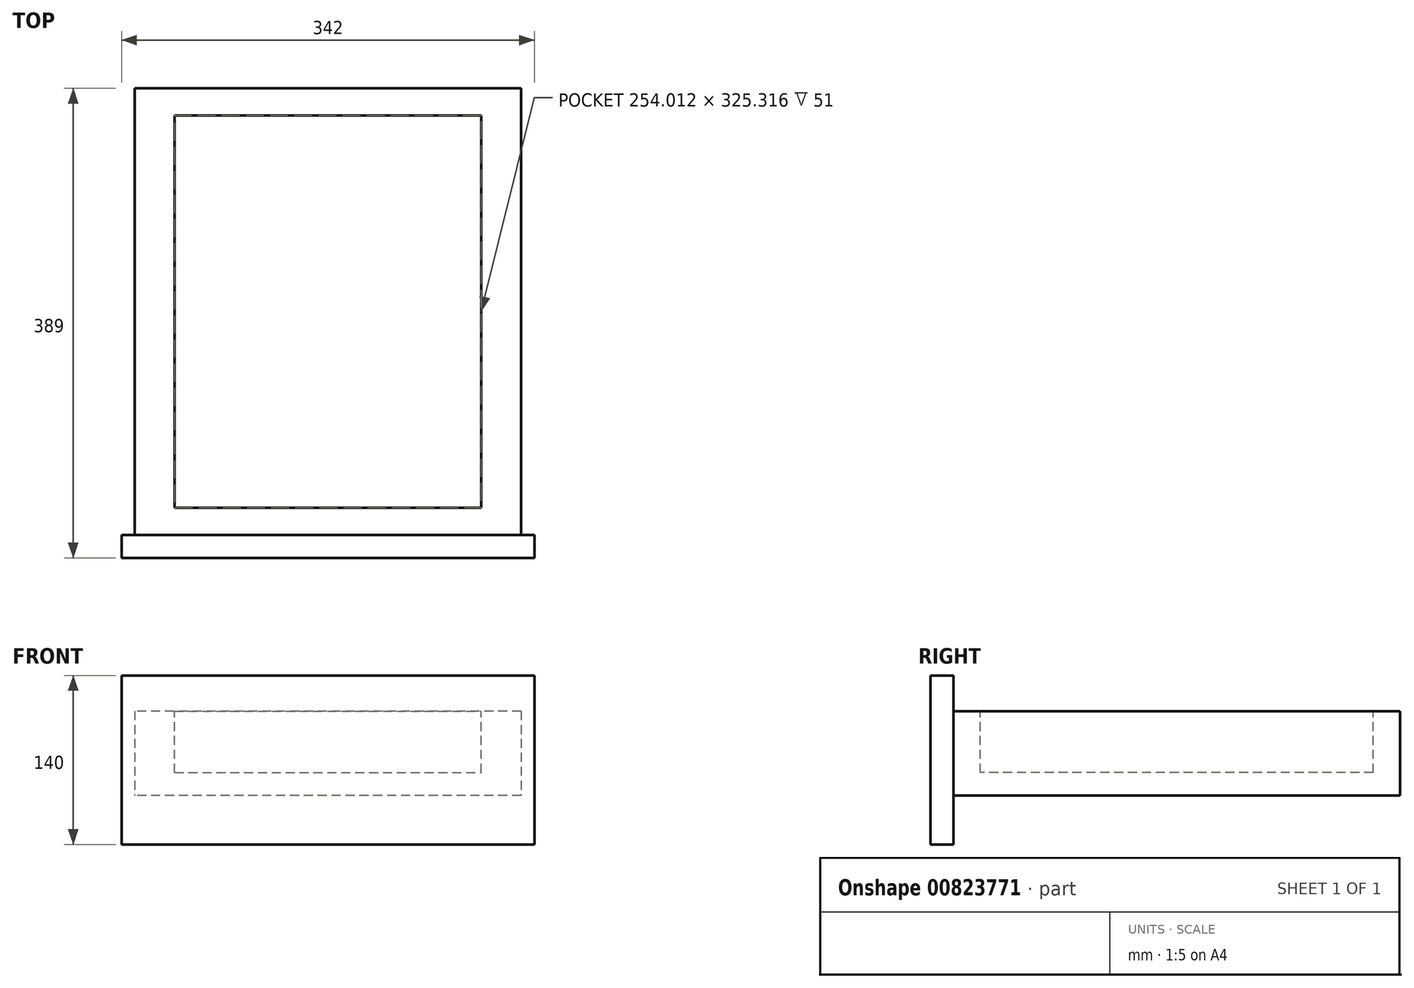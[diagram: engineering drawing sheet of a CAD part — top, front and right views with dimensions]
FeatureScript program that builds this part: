
annotation { "Feature Type Name" : "Feature", "Feature Type Description" : "" }
export const myFeature = defineFeature(function(context is Context, id is Id, definition is map)
    precondition{}
    {
        {
            var Q0;
            Q0=qCreatedBy(makeId("Top.planeOp"),FACE);
            var sketch = newSketch(context, id + "F0", { "sketchPlane" : qUnion([Q0])});
            skLineSegment(sketch, "E0.bottom", {"start": v(160, 185) * mm, "end": v(-160, 185) * mm});
            skLineSegment(sketch, "E0.top", {"start": v(160, -185) * mm, "end": v(-160, -185) * mm});
            skLineSegment(sketch, "E0.left", {"start": v(160, 185) * mm, "end": v(160, -185) * mm});
            skLineSegment(sketch, "E0.right", {"start": v(-160, 185) * mm, "end": v(-160, -185) * mm});
            skPoint(sketch, "E0.middle", {"position": v(0, 0) * mm});
            skSolve(sketch);
        }
        {
            var Q0;
            Q0=makeQuery(id+"F0.imprint","IMPRINT",FACE,{"disambiguationData":[TD([[makeQuery(id+"F0.imprint","IMPRINT",EDGE,{"derivedFrom":sQuery(id+"F0.wireOp",EDGE,"E0.bottom")}),1.0]])]});
            extrude(context, id + "F1", {"entities" : qUnion([Q0]), "depth" : 70 * mm, "offsetDistance" : 25 * mm});
        }
        {
            var Q0;
            Q0=makeQuery(id+"F1.opExtrude","CAP_FACE",FACE,{"disambiguationData":[OSD([sQuery(id+"F0.wireOp",EDGE,"E0.bottom"),sQuery(id+"F0.wireOp",EDGE,"E0.top"),sQuery(id+"F0.wireOp",EDGE,"E0.left"),sQuery(id+"F0.wireOp",EDGE,"E0.right")])],"isStart":false});
            var sketch = newSketch(context, id + "F2", { "sketchPlane" : qUnion([Q0])});
            skLineSegment(sketch, "E1.bottom", {"start": v(-127, 162.66) * mm, "end": v(127, 162.66) * mm});
            skLineSegment(sketch, "E1.top", {"start": v(-127, -162.66) * mm, "end": v(127, -162.66) * mm});
            skLineSegment(sketch, "E1.left", {"start": v(-127, 162.66) * mm, "end": v(-127, -162.66) * mm});
            skLineSegment(sketch, "E1.right", {"start": v(127, 162.66) * mm, "end": v(127, -162.66) * mm});
            skPoint(sketch, "E1.middle", {"position": v(0, 0) * mm});
            skSolve(sketch);
        }
        {
            var Q0;
            Q0=makeQuery(id+"F2.imprint","IMPRINT",FACE,{"disambiguationData":[TD([[makeQuery(id+"F2.imprint","IMPRINT",EDGE,{"derivedFrom":sQuery(id+"F2.wireOp",EDGE,"E1.bottom")}),-1.0]])]});
            extrude(context, id + "F3", {"entities" : qUnion([Q0]), "operationType" : NewBodyOperationType.REMOVE, "oppositeDirection" : true, "depth" : 51 * mm, "offsetDistance" : 25 * mm});
        }
        {
            var Q0;
            Q0=makeQuery(id+"F1.opExtrude","SWEPT_FACE",FACE,{"disambiguationData":[OSD([sQuery(id+"F0.wireOp",EDGE,"E0.top")])]});
            var sketch = newSketch(context, id + "F4", { "sketchPlane" : qUnion([Q0])});
            skLineSegment(sketch, "E2.bottom", {"start": v(171, 99.57) * mm, "end": v(-171, 99.57) * mm});
            skLineSegment(sketch, "E2.top", {"start": v(171, -40.43) * mm, "end": v(-171, -40.43) * mm});
            skLineSegment(sketch, "E2.left", {"start": v(171, 99.57) * mm, "end": v(171, -40.43) * mm});
            skLineSegment(sketch, "E2.right", {"start": v(-171, 99.57) * mm, "end": v(-171, -40.43) * mm});
            skPoint(sketch, "E2.middle", {"position": v(0, 29.57) * mm});
            skSolve(sketch);
        }
        {
            var Q0;
            Q0 = qSketchRegion(id + "F4", true);
            extrude(context, id + "F5", {"entities" : qUnion([Q0]), "operationType" : NewBodyOperationType.ADD, "depth" : 19 * mm, "offsetDistance" : 25 * mm});
        }
    });
